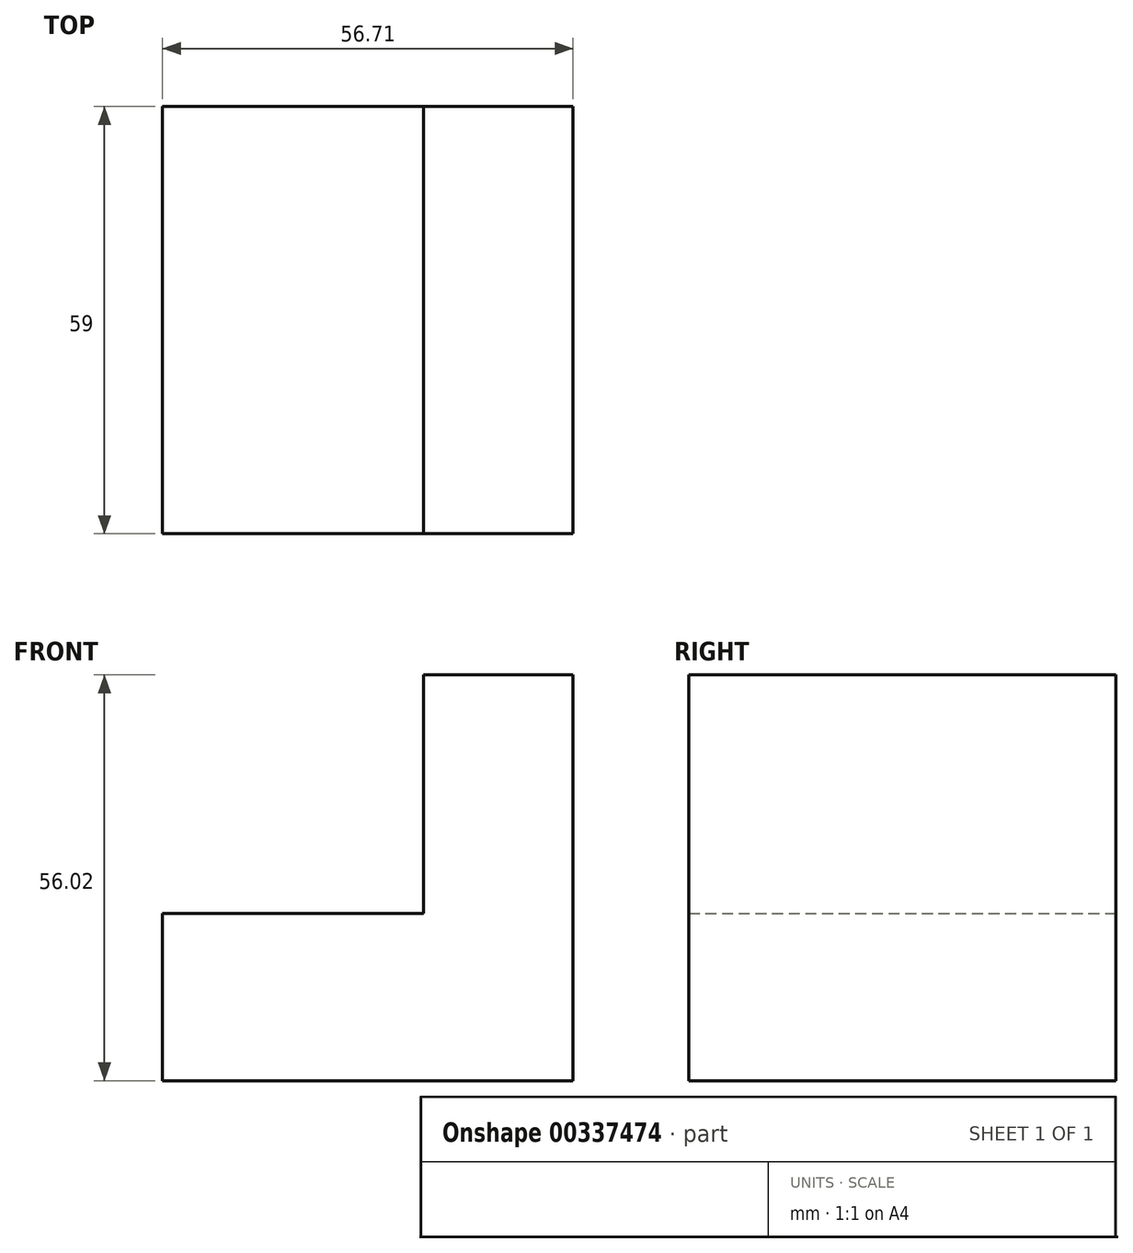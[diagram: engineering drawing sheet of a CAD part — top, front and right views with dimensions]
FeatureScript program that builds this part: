
annotation { "Feature Type Name" : "Feature", "Feature Type Description" : "" }
export const myFeature = defineFeature(function(context is Context, id is Id, definition is map)
    precondition{}
    {
        {
            var Q0;
            Q0=qCreatedBy(makeId("Front.planeOp"),FACE);
            var sketch = newSketch(context, id + "F0", { "sketchPlane" : qUnion([Q0])});
            skLineSegment(sketch, "E0.bottom", {"start": v(0, 0) * mm, "end": v(-56.71, 0) * mm});
            skLineSegment(sketch, "E0.top", {"start": v(0, 56.02) * mm, "end": v(-56.71, 56.02) * mm});
            skLineSegment(sketch, "E0.left", {"start": v(0, 0) * mm, "end": v(0, 56.02) * mm});
            skLineSegment(sketch, "E0.right", {"start": v(-56.71, 0) * mm, "end": v(-56.71, 56.02) * mm});
            skLineSegment(sketch, "E1.bottom", {"start": v(-56.71, 56.02) * mm, "end": v(-20.62, 56.02) * mm});
            skLineSegment(sketch, "E1.top", {"start": v(-56.71, 23.1) * mm, "end": v(-20.62, 23.1) * mm});
            skLineSegment(sketch, "E1.left", {"start": v(-56.71, 56.02) * mm, "end": v(-56.71, 23.1) * mm});
            skLineSegment(sketch, "E1.right", {"start": v(-20.62, 56.02) * mm, "end": v(-20.62, 23.1) * mm});
            skSolve(sketch);
        }
        {
            var Q0;
            Q0=makeQuery(id+"F0.imprint","IMPRINT",FACE,{"disambiguationData":[TD([[makeQuery(id+"F0.imprint","IMPRINT",EDGE,{"derivedFrom":sQuery(id+"F0.wireOp",EDGE,"E0.bottom")}),-1.0]])]});
            extrude(context, id + "F1", {"entities" : qUnion([Q0]), "depth" : 59 * mm});
        }
        {
            var Q0;
            Q0=qCreatedBy(makeId("Front.planeOp"),FACE);
            cPlane(context, id + "F2", {"entities" : qUnion([Q0]), "cplaneType" : CPlaneType.OFFSET, "offset" : 30 * mm, "width" : 150 * mm, "height" : 150 * mm});
        }
    });
